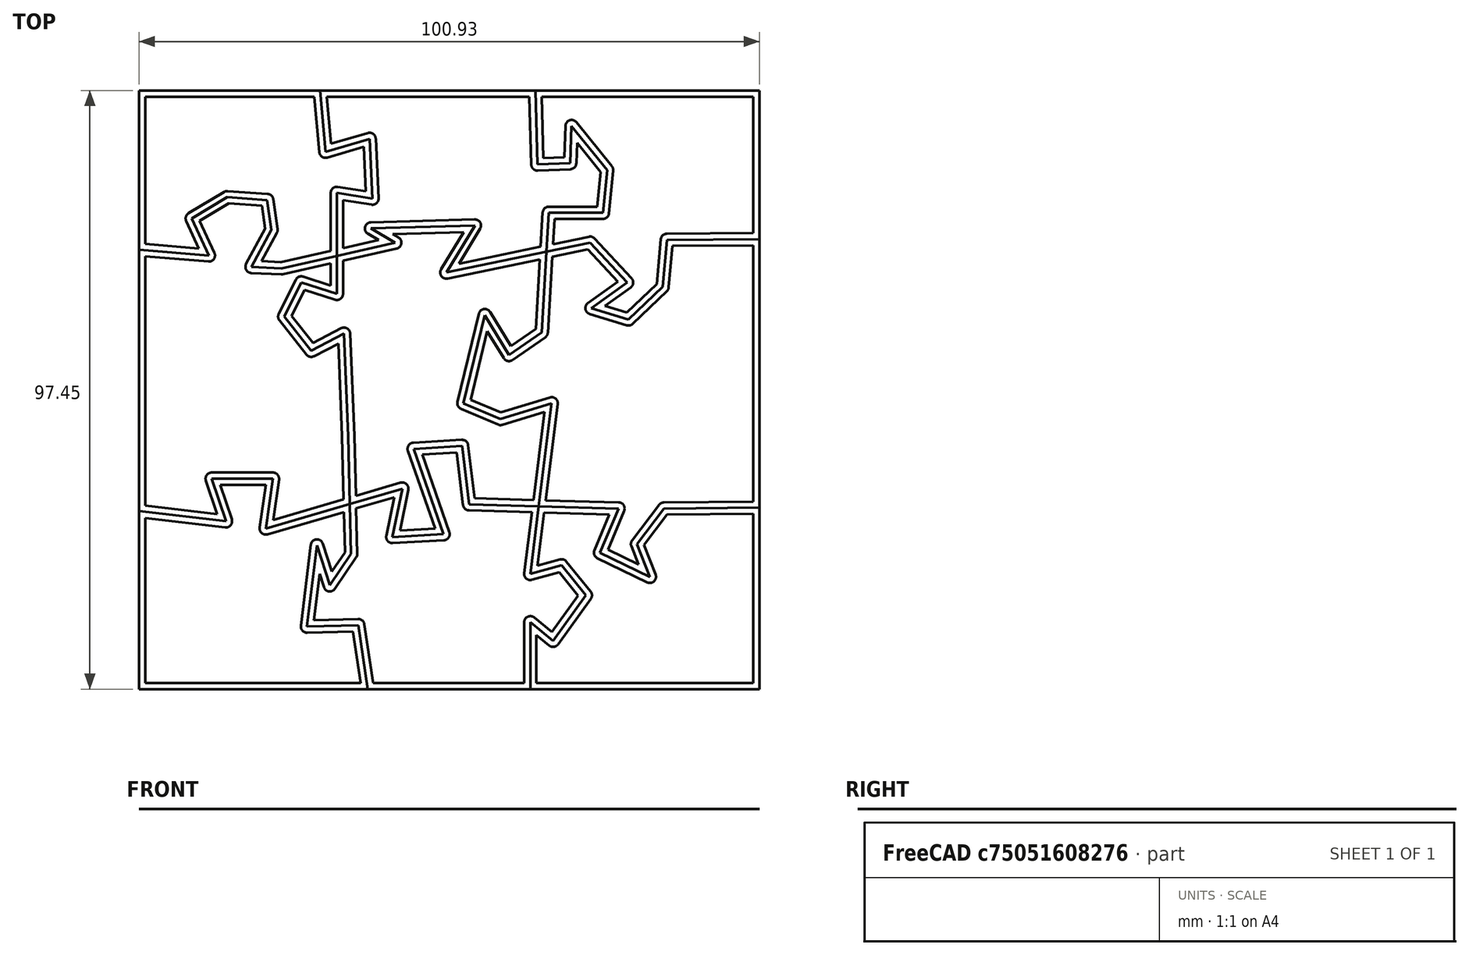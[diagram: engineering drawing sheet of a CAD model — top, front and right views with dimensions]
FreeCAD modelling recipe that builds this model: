
FCSTD DOCUMENT  (FreeCAD 0.17R8448 (Git))
Label: offset-face-example
License: All rights reserved
LicenseURL: http://en.wikipedia.org/wiki/All_rights_reserved
objects: Sketcher::SketchObject×2, Part::FeaturePython×2, Part::Face×1, Part::Offset2D×1
note: 6 computed .brp shape members not serialized (recipe doc carries the construction recipe); baked Part::Feature solids carry a one-line shape summary decoded from their .brp

FEATURE [Sketcher::SketchObject] Sketch  label="Sketch - outline"
  sketch-geometry (4):
    g0: LineSegment StartX=-66.4359 StartY=46.9912 StartZ=0 EndX=34.4911 EndY=46.9912 EndZ=0
    g1: LineSegment StartX=34.4911 StartY=46.9912 StartZ=0 EndX=34.4911 EndY=-50.4635 EndZ=0
    g2: LineSegment StartX=34.4911 StartY=-50.4635 StartZ=0 EndX=-66.4359 EndY=-50.4635 EndZ=0
    g3: LineSegment StartX=-66.4359 StartY=-50.4635 StartZ=0 EndX=-66.4359 EndY=46.9912 EndZ=0
  constraints (8):
    c: Coincident(g0,g1)
    c: Coincident(g1,g2)
    c: Coincident(g2,g3)
    c: Coincident(g3,g0)
    c: Horizontal(g0)
    c: Horizontal(g2)
    c: Vertical(g1)
    c: Vertical(g3)
FEATURE [Part::Face] Face
  FaceMakerClass = Part::FaceMakerCheese
  Sources = -> [Sketch]
FEATURE [Sketcher::SketchObject] Sketch001  label="Sketch001 - splitters"
  sketch-geometry (68):
    g0: LineSegment StartX=-37.5004 StartY=52.3154 StartZ=0 EndX=-36.1115 EndY=37.0374 EndZ=0
    g1: LineSegment StartX=-36.1115 StartY=37.0374 StartZ=0 EndX=-28.9355 EndY=39.1208 EndZ=0
    g2: LineSegment StartX=-28.9355 StartY=39.1208 StartZ=0 EndX=-28.4725 EndY=29.3985 EndZ=0
    g3: LineSegment StartX=-28.4725 StartY=29.3985 StartZ=0 EndX=-34.2596 EndY=30.3244 EndZ=0
    g4: LineSegment StartX=-34.2596 StartY=30.3244 StartZ=0 EndX=-34.2596 EndY=13.889 EndZ=0
    g5: LineSegment StartX=-34.2596 StartY=13.889 StartZ=0 EndX=-40.0467 EndY=15.7409 EndZ=0
    g6: LineSegment StartX=-40.0467 StartY=15.7409 StartZ=0 EndX=-42.8245 EndY=10.1853 EndZ=0
    g7: LineSegment StartX=-42.8245 StartY=10.1853 StartZ=0 EndX=-38.4263 EndY=4.62968 EndZ=0
    g8: LineSegment StartX=-38.4263 StartY=4.62968 StartZ=0 EndX=-33.1022 EndY=7.40749 EndZ=0
    g9: LineSegment StartX=-33.1022 StartY=7.40749 StartZ=0 EndX=-32.4078 EndY=-9.25936 EndZ=0
    g10: LineSegment StartX=-32.4078 StartY=-9.25936 StartZ=0 EndX=-31.9448 EndY=-28.4725 EndZ=0
    g11: LineSegment StartX=-31.9448 StartY=-28.4725 StartZ=0 EndX=-35.417 EndY=-33.5652 EndZ=0
    g12: LineSegment StartX=-35.417 StartY=-33.5652 StartZ=0 EndX=-37.5004 EndY=-27.0836 EndZ=0
    g13: LineSegment StartX=-37.5004 StartY=-27.0836 StartZ=0 EndX=-39.1208 EndY=-40.2782 EndZ=0
    g14: LineSegment StartX=-39.1208 StartY=-40.2782 StartZ=0 EndX=-30.7874 EndY=-40.0467 EndZ=0
    g15: LineSegment StartX=-30.7874 StartY=-40.0467 StartZ=0 EndX=-28.241 EndY=-56.9451 EndZ=0
    g16: LineSegment StartX=-76.8527 StartY=21.991 StartZ=0 EndX=-55.0932 EndY=20.1391 EndZ=0
    g17: LineSegment StartX=-55.0932 StartY=20.1391 StartZ=0 EndX=-57.871 EndY=26.1577 EndZ=0
    g18: LineSegment StartX=-57.871 StartY=26.1577 StartZ=0 EndX=-52.0839 EndY=29.6299 EndZ=0
    g19: LineSegment StartX=-52.0839 StartY=29.6299 StartZ=0 EndX=-45.6023 EndY=29.167 EndZ=0
    g20: LineSegment StartX=-45.6023 StartY=29.167 StartZ=0 EndX=-44.9079 EndY=24.3058 EndZ=0
    g21: LineSegment StartX=-44.9079 StartY=24.3058 StartZ=0 EndX=-48.1487 EndY=18.2872 EndZ=0
    g22: LineSegment StartX=-48.1487 StartY=18.2872 StartZ=0 EndX=-43.2875 EndY=18.0557 EndZ=0
    g23: LineSegment StartX=-43.2875 StartY=18.0557 StartZ=0 EndX=-24.7688 EndY=22.2225 EndZ=0
    g24: LineSegment StartX=-24.7688 StartY=22.2225 StartZ=0 EndX=-28.704 EndY=24.5373 EndZ=0
    g25: LineSegment StartX=-28.704 StartY=24.5373 StartZ=0 EndX=-11.8057 EndY=25.0003 EndZ=0
    g26: LineSegment StartX=-11.8057 StartY=25.0003 StartZ=0 EndX=-16.4354 EndY=17.3613 EndZ=0
    g27: LineSegment StartX=-16.4354 StartY=17.3613 StartZ=0 EndX=6.94452 EndY=22.2225 EndZ=0
    g28: LineSegment StartX=6.94452 StartY=22.2225 StartZ=0 EndX=12.9631 EndY=15.7409 EndZ=0
    g29: LineSegment StartX=12.9631 StartY=15.7409 StartZ=0 EndX=7.176 EndY=11.5742 EndZ=0
    g30: LineSegment StartX=7.176 StartY=11.5742 StartZ=0 EndX=13.1946 EndY=9.72232 EndZ=0
    g31: LineSegment StartX=13.1946 StartY=9.72232 StartZ=0 EndX=18.7502 EndY=15.0465 EndZ=0
    g32: LineSegment StartX=18.7502 StartY=15.0465 StartZ=0 EndX=19.4447 EndY=22.6854 EndZ=0
    g33: LineSegment StartX=19.4447 StartY=22.6854 StartZ=0 EndX=47.4542 EndY=22.9169 EndZ=0
    g34: LineSegment StartX=-2.08335 StartY=50.9265 StartZ=0 EndX=-1.62039 EndY=34.9541 EndZ=0
    g35: LineSegment StartX=-1.62039 StartY=34.9541 StartZ=0 EndX=3.70375 EndY=35.1856 EndZ=0
    g36: LineSegment StartX=3.70375 StartY=35.1856 StartZ=0 EndX=3.93523 EndY=41.2041 EndZ=0
    g37: LineSegment StartX=3.93523 StartY=41.2041 StartZ=0 EndX=9.72233 EndY=34.0281 EndZ=0
    g38: LineSegment StartX=9.72233 StartY=34.0281 StartZ=0 EndX=9.02787 EndY=27.0836 EndZ=0
    g39: LineSegment StartX=9.02787 StartY=27.0836 StartZ=0 EndX=0.231484 EndY=27.0836 EndZ=0
    g40: LineSegment StartX=0.231484 StartY=27.0836 StartZ=0 EndX=-0.925931 EndY=7.63897 EndZ=0
    g41: LineSegment StartX=-0.925931 StartY=7.63897 StartZ=0 EndX=-6.25007 EndY=3.93522 EndZ=0
    g42: LineSegment StartX=-6.25007 StartY=3.93522 StartZ=0 EndX=-10.1853 EndY=10.4168 EndZ=0
    g43: LineSegment StartX=-10.1853 StartY=10.4168 StartZ=0 EndX=-13.6575 EndY=-3.93523 EndZ=0
    g44: LineSegment StartX=-13.6575 StartY=-3.93523 StartZ=0 EndX=-7.63897 EndY=-6.48155 EndZ=0
    g45: LineSegment StartX=-7.63897 StartY=-6.48155 StartZ=0 EndX=0.694443 EndY=-3.93523 EndZ=0
    g46: LineSegment StartX=0.694443 StartY=-3.93523 StartZ=0 EndX=-2.7778 EndY=-31.7133 EndZ=0
    g47: LineSegment StartX=-2.7778 StartY=-31.7133 StartZ=0 EndX=2.31484 EndY=-30.3244 EndZ=0
    g48: LineSegment StartX=2.31484 StartY=-30.3244 StartZ=0 EndX=6.25008 EndY=-35.1856 EndZ=0
    g49: LineSegment StartX=6.25008 StartY=-35.1856 StartZ=0 EndX=0.925935 EndY=-42.593 EndZ=0
    g50: LineSegment StartX=0.925935 StartY=-42.593 StartZ=0 EndX=-2.7778 EndY=-39.5838 EndZ=0
    g51: LineSegment StartX=-2.7778 StartY=-39.5838 StartZ=0 EndX=-2.7778 EndY=-57.1765 EndZ=0
    g52: LineSegment StartX=-73.6119 StartY=-20.6021 StartZ=0 EndX=-52.3154 EndY=-23.1484 EndZ=0
    g53: LineSegment StartX=-52.3154 StartY=-23.1484 StartZ=0 EndX=-54.6302 EndY=-16.2039 EndZ=0
    g54: LineSegment StartX=-54.6302 StartY=-16.2039 StartZ=0 EndX=-44.6764 EndY=-16.2039 EndZ=0
    g55: LineSegment StartX=-44.6764 StartY=-16.2039 StartZ=0 EndX=-45.8338 EndY=-24.3058 EndZ=0
    g56: LineSegment StartX=-45.8338 StartY=-24.3058 StartZ=0 EndX=-23.6114 EndY=-17.8243 EndZ=0
    g57: LineSegment StartX=-23.6114 StartY=-17.8243 StartZ=0 EndX=-25.2317 EndY=-25.6947 EndZ=0
    g58: LineSegment StartX=-25.2317 StartY=-25.6947 StartZ=0 EndX=-16.8983 EndY=-25.2318 EndZ=0
    g59: LineSegment StartX=-16.8983 StartY=-25.2318 StartZ=0 EndX=-21.7595 EndY=-11.3427 EndZ=0
    g60: LineSegment StartX=-21.7595 StartY=-11.3427 StartZ=0 EndX=-13.889 EndY=-10.8797 EndZ=0
    g61: LineSegment StartX=-13.889 StartY=-10.8797 StartZ=0 EndX=-12.7316 EndY=-20.3706 EndZ=0
    g62: LineSegment StartX=-12.7316 StartY=-20.3706 StartZ=0 EndX=11.5742 EndY=-21.065 EndZ=0
    g63: LineSegment StartX=11.5742 StartY=-21.065 StartZ=0 EndX=8.56491 EndY=-28.241 EndZ=0
    g64: LineSegment StartX=8.56491 StartY=-28.241 StartZ=0 EndX=16.6669 EndY=-32.1763 EndZ=0
    g65: LineSegment StartX=16.6669 StartY=-32.1763 StartZ=0 EndX=14.5835 EndY=-26.8521 EndZ=0
    g66: LineSegment StartX=14.5835 StartY=-26.8521 StartZ=0 EndX=18.9817 EndY=-21.065 EndZ=0
    g67: LineSegment StartX=18.9817 StartY=-21.065 StartZ=0 EndX=44.9079 EndY=-20.8336 EndZ=0
  constraints (64):
    c: Coincident(g0,g1)
    c: Coincident(g1,g2)
    c: Coincident(g2,g3)
    c: Coincident(g3,g4)
    c: Coincident(g4,g5)
    c: Coincident(g5,g6)
    c: Coincident(g6,g7)
    c: Coincident(g7,g8)
    c: Coincident(g8,g9)
    c: Coincident(g9,g10)
    c: Coincident(g10,g11)
    c: Coincident(g11,g12)
    c: Coincident(g12,g13)
    c: Coincident(g13,g14)
    c: Coincident(g14,g15)
    c: Coincident(g16,g17)
    c: Coincident(g17,g18)
    c: Coincident(g18,g19)
    c: Coincident(g19,g20)
    c: Coincident(g20,g21)
    c: Coincident(g21,g22)
    c: Coincident(g22,g23)
    c: Coincident(g23,g24)
    c: Coincident(g24,g25)
    c: Coincident(g25,g26)
    c: Coincident(g26,g27)
    c: Coincident(g27,g28)
    c: Coincident(g28,g29)
    c: Coincident(g29,g30)
    c: Coincident(g30,g31)
    c: Coincident(g31,g32)
    c: Coincident(g32,g33)
    c: Coincident(g34,g35)
    c: Coincident(g35,g36)
    c: Coincident(g36,g37)
    c: Coincident(g37,g38)
    c: Coincident(g38,g39)
    c: Coincident(g39,g40)
    c: Coincident(g40,g41)
    c: Coincident(g41,g42)
    c: Coincident(g42,g43)
    c: Coincident(g43,g44)
    c: Coincident(g44,g45)
    c: Coincident(g45,g46)
    c: Coincident(g46,g47)
    c: Coincident(g47,g48)
    c: Coincident(g48,g49)
    c: Coincident(g49,g50)
    c: Coincident(g50,g51)
    c: Coincident(g52,g53)
    c: Coincident(g53,g54)
    c: Coincident(g54,g55)
    c: Coincident(g55,g56)
    c: Coincident(g56,g57)
    c: Coincident(g57,g58)
    c: Coincident(g58,g59)
    c: Coincident(g59,g60)
    c: Coincident(g60,g61)
    c: Coincident(g61,g62)
    c: Coincident(g62,g63)
    c: Coincident(g63,g64)
    c: Coincident(g64,g65)
    c: Coincident(g65,g66)
    c: Coincident(g66,g67)
FEATURE [Part::FeaturePython] BooleanFragments  # WARN: FeaturePython — macro-defined, semantics opaque (R4)
  Mode = 0
  Objects = -> [Sketch001]
  Tolerance = 0
FEATURE [Part::FeaturePython] Slice  label="Slice - PuzzleFaces"  # WARN: FeaturePython — macro-defined, semantics opaque (R4)
  Base = -> Face
  Mode = 1
  Tolerance = 0
  Tools = -> [BooleanFragments]
FEATURE [Part::Offset2D] Offset2D
  Fill = true
  Intersection = false
  Join = 0
  Mode = 1
  SelfIntersection = false
  Source = -> Slice
  Value = -1
